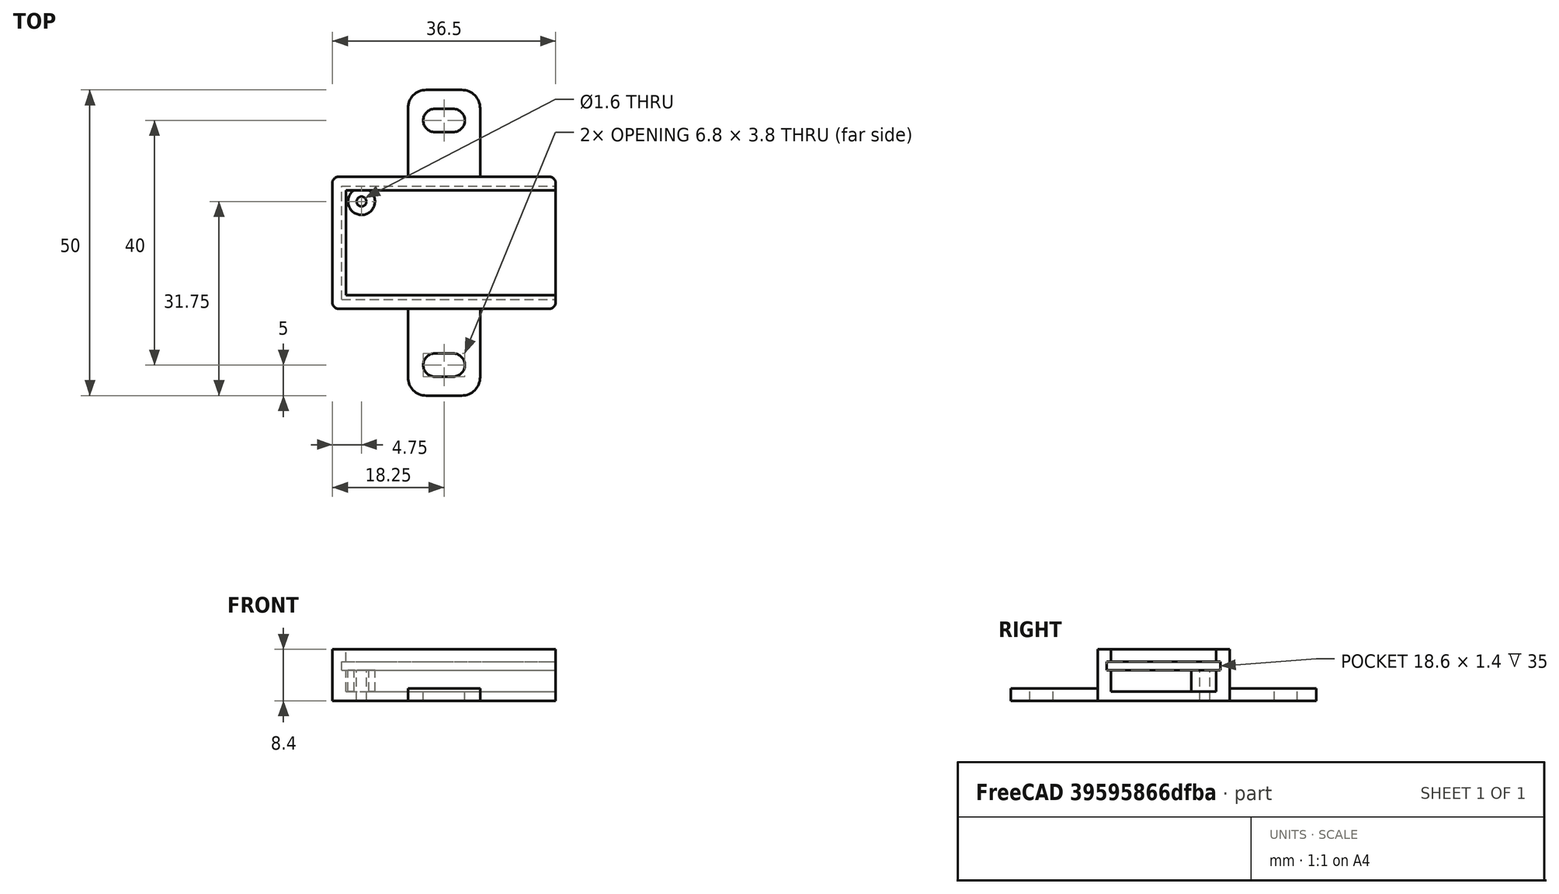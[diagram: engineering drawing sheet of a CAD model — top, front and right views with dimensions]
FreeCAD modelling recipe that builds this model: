
FCSTD DOCUMENT  (FreeCAD 0.19R23578 (Git))
Label: stdz-1810-ty_ultrasound
License: FreeArt
LicenseURL: http://artlibre.org/licence/lal
objects: Part::Box×3, Part::MultiFuse×3, Part::Cylinder×2, Part::Cut×2, Spreadsheet::Sheet×1, Part::Fillet×1, Part::Feature×1, App::Part×1
note: 12 computed .brp shape members not serialized (recipe doc carries the construction recipe); baked Part::Feature solids carry a one-line shape summary decoded from their .brp

FEATURE [Spreadsheet::Sheet] Spreadsheet  label="p"
  cells = A1=pcb_x; B1(pcb_x)=35; A2=pcb_y; B2(pcb_y)=18.6; A3=pcb_z; B3(pcb_z)=1.4; A4=pcb_under; B4(pcb_under)=3.5; A5=side_wall; B5(side_wall)=1.5; A6=pcb_side_lane; B6(pcb_side_lane)=0.7; A7=bottom_wall; B7(bottom_wall)=1.5; A8=pcb_above; B8(pcb_above)=2; A9=hole_r; B9(hole_r)=0.8; A10=stand_r; B10(stand_r)=2.2; A11=hole_dist_x; B11(hole_dist_x)=29; A12=hole_dist_y; B12(hole_dist_y)=13.5
FEATURE [Part::Box] Box  label="external cube"
  AttacherType = Attacher::AttachEngine3D
  Height = 8.4
  Length = 36.5
  Width = 21.6
  expr: Length = <<p>>.pcb_x + <<p>>.side_wall
  expr: Width = <<p>>.pcb_y + 2 * <<p>>.side_wall
  expr: Height = <<p>>.bottom_wall + <<p>>.pcb_under + <<p>>.pcb_z + <<p>>.pcb_above
FEATURE [Part::Box] Box006  label="internal cube"
  AttacherType = Attacher::AttachEngine3D
  Height = 6.9
  Length = 35.1
  Placement = pos=(2.2,2.2,1.5) rot=(0,0,1;0rad)
  Width = 17.2
  expr: Length = <<p>>.pcb_x - 2 * <<p>>.pcb_side_lane + <<p>>.side_wall
  expr: Width = <<p>>.pcb_y - 2 * <<p>>.pcb_side_lane
  expr: Height = <<p>>.pcb_under + <<p>>.pcb_z + <<p>>.pcb_above
  expr: .Placement.Base.z = <<p>>.bottom_wall
  expr: .Placement.Base.x = <<p>>.side_wall + <<p>>.pcb_side_lane
  expr: .Placement.Base.y = <<p>>.side_wall + <<p>>.pcb_side_lane
FEATURE [Part::Box] Box007  label="pcb extract cube"
  AttacherType = Attacher::AttachEngine3D
  Height = 1.4
  Length = 35
  Placement = pos=(1.5,1.5,5) rot=(0,0,1;0rad)
  Width = 18.6
  expr: Height = <<p>>.pcb_z
  expr: .Placement.Base.z = <<p>>.bottom_wall + <<p>>.pcb_under
  expr: Width = <<p>>.pcb_y
  expr: Length = <<p>>.pcb_x
  expr: .Placement.Base.x = <<p>>.side_wall
  expr: .Placement.Base.y = <<p>>.side_wall
FEATURE [Part::MultiFuse] Fusion  label="extract fusion"
  Shapes = -> [Box006,Box007]
FEATURE [Part::Fillet] Fillet  label="external fillet"
  Base = -> Box
  Edges = 4 edges r=1: [Edge1,Edge3,Edge5,Edge7]
FEATURE [Part::Cylinder] Cylinder001  label="hole"
  Angle = 360
  AttacherType = Attacher::AttachEngine3D
  Height = 10
  Placement = pos=(4.75,17.55,0) rot=(0,0,1;0rad)
  Radius = 0.8
  expr: .Placement.Base.x = (<<p>>.side_wall + <<p>>.pcb_x - <<p>>.hole_dist_x) / 2 + 1
  expr: Radius = <<p>>.hole_r
  expr: .Placement.Base.y = (2 * <<p>>.side_wall + <<p>>.pcb_y + <<p>>.hole_dist_y) / 2
FEATURE [Part::Cylinder] Cylinder003  label="stand"
  Angle = 360
  AttacherType = Attacher::AttachEngine3D
  Height = 5
  Placement = pos=(4.75,17.55,0) rot=(0,0,1;0rad)
  Radius = 2.2
  expr: .Placement.Base.x = (<<p>>.side_wall + <<p>>.pcb_x - <<p>>.hole_dist_x) / 2 + 1
  expr: Height = <<p>>.bottom_wall + <<p>>.pcb_under
  expr: .Placement.Base.y = (2 * <<p>>.side_wall + <<p>>.pcb_y + <<p>>.hole_dist_y) / 2
  expr: Radius = <<p>>.stand_r
FEATURE [Part::Feature] Cut002001  label="attach plane y dir001"
  Placement = pos=(12.35,-14.2,0) rot=(0,0,1;0rad)
  shape: bbox 11.8 x 50 x 2 mm, 20 faces (baked)
FEATURE [Part::MultiFuse] Fusion001  label="solid fusion"
  Shapes = -> [Fillet,Cut002001]
FEATURE [Part::Cut] Cut  label="base body cut"
  Base = -> Fusion001
  Tool = -> Fusion
FEATURE [Part::MultiFuse] Fusion004  label="body fusion"
  Shapes = -> [Cut,Cylinder003]
FEATURE [Part::Cut] Cut002003  label="body cut"
  Base = -> Fusion004
  Tool = -> Cylinder001
FEATURE [App::Part] Part  label="stdz-1810-ty_ultrasound pcb box part"
  Group = -> [Box,Fillet,Fusion001,Fusion,Box007,Box006,Cut,Cylinder003,Fusion004,Cylinder001,Cut002003]
  Origin = -> Origin
